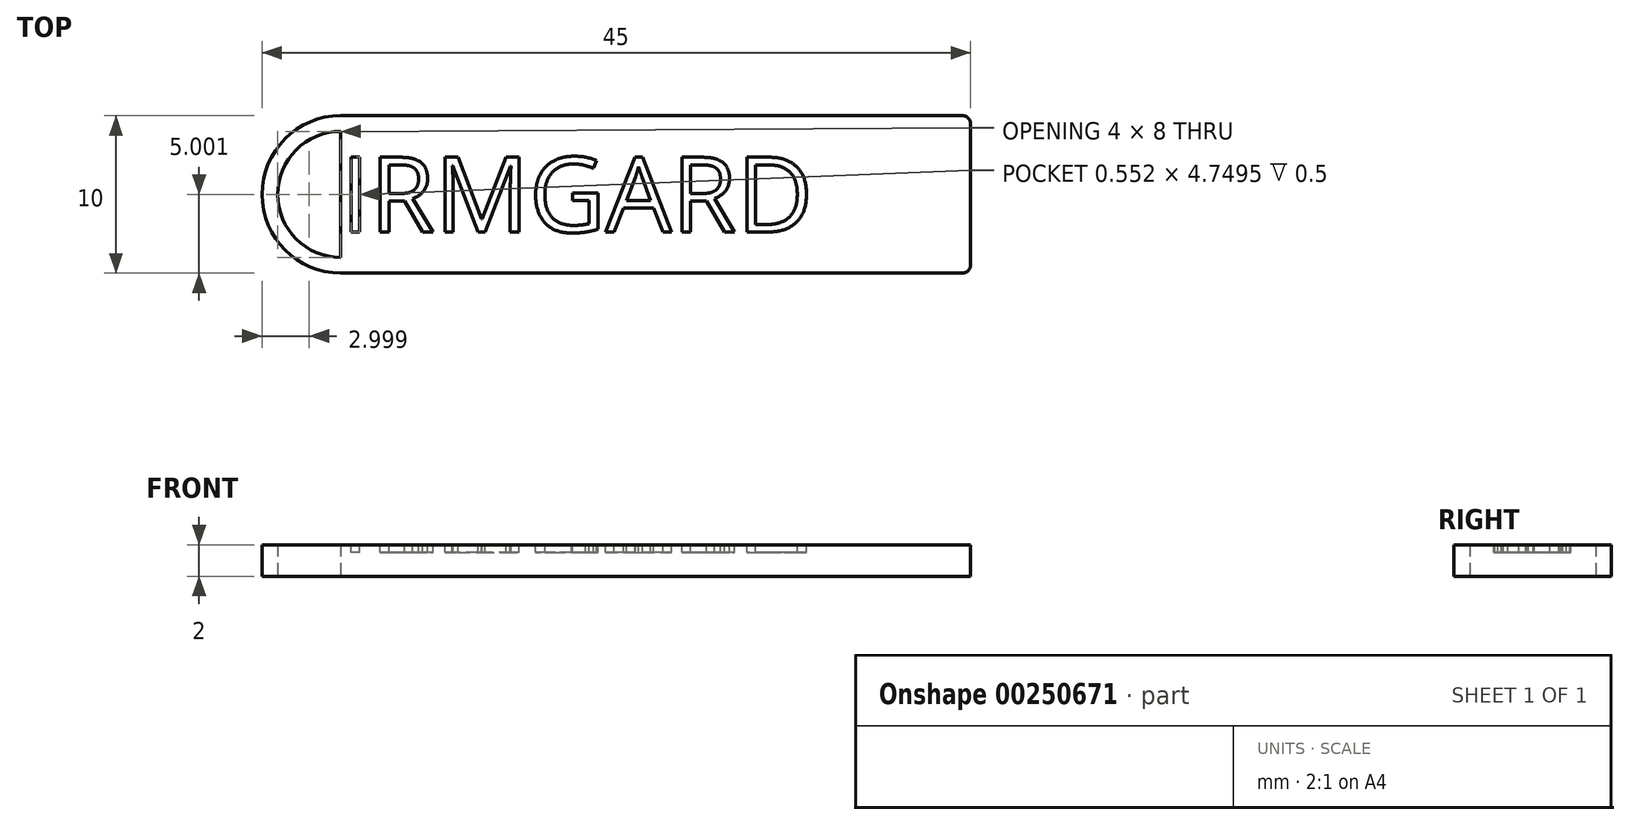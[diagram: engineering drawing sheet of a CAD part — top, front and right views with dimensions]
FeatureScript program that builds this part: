
annotation { "Feature Type Name" : "Feature", "Feature Type Description" : "" }
export const myFeature = defineFeature(function(context is Context, id is Id, definition is map)
    precondition{}
    {
        {
            var Q0;
            Q0=qCreatedBy(makeId("Top.planeOp"),FACE);
            var sketch = newSketch(context, id + "F0", { "sketchPlane" : qUnion([Q0])});
            skLineSegment(sketch, "E0.bottom", {"start": v(-5.27, 3.22) * mm, "end": v(34.73, 3.22) * mm});
            skLineSegment(sketch, "E0.top", {"start": v(-5.27, -6.78) * mm, "end": v(34.73, -6.78) * mm});
            skLineSegment(sketch, "E0.left", {"start": v(-5.27, 3.22) * mm, "end": v(-5.27, -6.78) * mm});
            skLineSegment(sketch, "E0.right", {"start": v(34.73, 3.22) * mm, "end": v(34.73, -6.78) * mm});
            skArc(sketch, "E1", {"start": v(-5.27, 3.22) * mm, "mid": v(-10.27, -1.78) * mm, "end": v(-5.27, -6.78) * mm});
            skArc(sketch, "E2", {"start": v(-5.27, 2.22) * mm, "mid": v(-9.27, -1.78) * mm, "end": v(-5.27, -5.78) * mm});
            skSolve(sketch);
        }
        {
            var Q0;
            Q0=qSketchRegion(id+"F0",true);
            extrude(context, id + "F4", {"entities" : qUnion([Q0]), "depth" : 2 * mm});
        }
        {
            var Q0;
            Q0=makeQuery(id+"F4.opExtrude","SWEPT_EDGE",EDGE,{"disambiguationData":[OSD([sQuery(id+"F0.wireOp",EDGE,"E0.top"),sQuery(id+"F0.wireOp",EDGE,"E0.right")])]});
            var Q1;
            Q1=makeQuery(id+"F4.opExtrude","SWEPT_EDGE",EDGE,{"disambiguationData":[OSD([sQuery(id+"F0.wireOp",EDGE,"E0.bottom"),sQuery(id+"F0.wireOp",EDGE,"E0.right")])]});
            fillet(context, id + "F1", {"entities" : qUnion([Q0, Q1]), "radius" : 0.5 * mm, "tangentPropagation" : true, "allowEdgeOverflow" : false});
        }
        {
            var Q0;
            Q0=makeQuery(id+"F4.opExtrude","CAP_FACE",FACE,{"disambiguationData":[OSD([sQuery(id+"F0.wireOp",EDGE,"E0.bottom"),sQuery(id+"F0.wireOp",EDGE,"E0.top"),sQuery(id+"F0.wireOp",EDGE,"E0.left"),sQuery(id+"F0.wireOp",EDGE,"E0.right"),sQuery(id+"F0.wireOp",EDGE,"E1"),sQuery(id+"F0.wireOp",EDGE,"E2")])],"isStart":false});
            var sketch = newSketch(context, id + "F2", { "sketchPlane" : qUnion([Q0])});
            skText(sketch, "E3", { "text": "IRMGARD", "fontName": "OpenSans-Regular.ttf"});
            skPoint(sketch, "E4", {"position": v(-5.27, -1.78) * mm});
            skPoint(sketch, "E5", {"position": v(34.73, -1.78) * mm});
            const initialGuessF2  = {"E3": [-0.00527, -0.00417, 1, 0, 0.00479]};
            skSetInitialGuess(sketch, initialGuessF2);
            skSolve(sketch);
        }
        {
            var Q0;
            Q0 = qSketchRegion(id + "F2", true);
            extrude(context, id + "F3", {"entities" : qUnion([Q0]), "operationType" : NewBodyOperationType.REMOVE, "oppositeDirection" : true, "depth" : 0.5 * mm});
        }
    });
